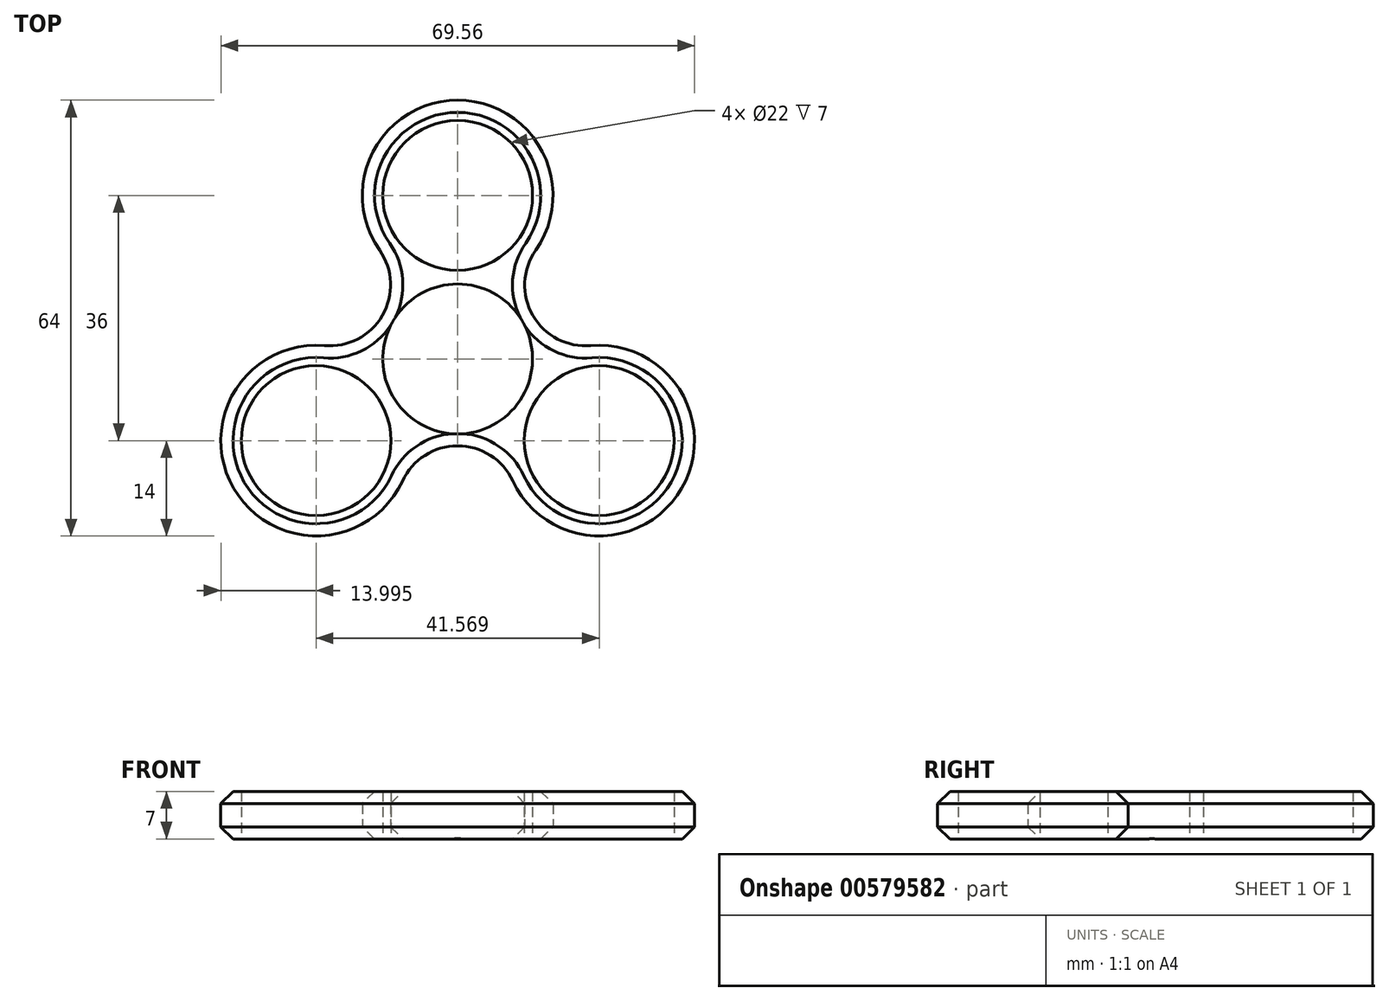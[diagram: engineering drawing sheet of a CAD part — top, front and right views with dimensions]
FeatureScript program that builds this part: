
annotation { "Feature Type Name" : "Feature", "Feature Type Description" : "" }
export const myFeature = defineFeature(function(context is Context, id is Id, definition is map)
    precondition{}
    {
        {
            var Q0;
            Q0=qCreatedBy(makeId("Top.planeOp"),FACE);
            var sketch = newSketch(context, id + "F0", { "sketchPlane" : qUnion([Q0])});
            skCircle(sketch, "E0", {"center": v(0, 0) * mm, "radius": 11 * mm});
            skLineSegment(sketch, "E1", {"start": v(0, 0) * mm, "end": v(0, 11) * mm});
            skCircle(sketch, "E2", {"center": v(0, 24) * mm, "radius": 11 * mm});
            skArc(sketch, "E3.0", {"start": v(11.47, 15.97) * mm, "mid": v(0, 38) * mm, "end": v(-11.47, 15.97) * mm});
            skPoint(sketch, "E4", {"position": v(0, 11) * mm});
            skPoint(sketch, "E5", {"position": v(-12.12, 17) * mm});
            skPoint(sketch, "E6", {"position": v(13, 19.5) * mm});
            skArc(sketch, "E7.1.0", {"start": v(-19.56, 1.95) * mm, "mid": v(-32.9, -19) * mm, "end": v(-8.1, -17.92) * mm});
            skCircle(sketch, "E7.1.1", {"center": v(-20.78, -12) * mm, "radius": 11 * mm});
            skArc(sketch, "E7.2.0", {"start": v(8.1, -17.92) * mm, "mid": v(32.9, -19) * mm, "end": v(19.56, 1.95) * mm});
            skCircle(sketch, "E7.2.1", {"center": v(20.78, -12) * mm, "radius": 11 * mm});
            skPoint(sketch, "E8.1.0", {"position": v(-8.66, -19) * mm});
            skPoint(sketch, "E8.2.0", {"position": v(20.78, 2) * mm});
            skPoint(sketch, "E9.MirrorP", {"position": v(12.12, 17) * mm});
            skPoint(sketch, "E10.1.0", {"position": v(-20.78, 2) * mm});
            skPoint(sketch, "E10.2.0", {"position": v(8.66, -19) * mm});
            skLineSegment(sketch, "E11", {"start": v(-11.05, 6.38) * mm, "end": v(-11.26, 6.5) * mm});
            skPoint(sketch, "E12", {"position": v(-11.26, 6.5) * mm});
            skLineSegment(sketch, "E13", {"start": v(0, 24) * mm, "end": v(-9.01, 17.7) * mm});
            skLineSegment(sketch, "E14.MirrorCS", {"start": v(-20.78, -12) * mm, "end": v(-19.83, -1.04) * mm});
            skPoint(sketch, "E15.orphan", {"position": v(-3.47, 10.44) * mm});
            skArc(sketch, "E16", {"start": v(-11.47, 15.97) * mm, "mid": v(-11.05, 6.38) * mm, "end": v(-19.56, 1.95) * mm});
            skArc(sketch, "E17.1.0", {"start": v(-8.1, -17.92) * mm, "mid": v(0, -12.76) * mm, "end": v(8.1, -17.92) * mm});
            skArc(sketch, "E17.2.0", {"start": v(19.56, 1.95) * mm, "mid": v(11.05, 6.38) * mm, "end": v(11.47, 15.97) * mm});
            skPoint(sketch, "E18.orphan", {"position": v(-10.78, -2.21) * mm});
            skPoint(sketch, "E19.orphan", {"position": v(3.47, 10.44) * mm});
            skPoint(sketch, "E20.orphan", {"position": v(10.78, -2.21) * mm});
            skPoint(sketch, "E21.orphan", {"position": v(7.3, -8.23) * mm});
            skPoint(sketch, "E22.orphan", {"position": v(-7.3, -8.23) * mm});
            skLineSegment(sketch, "E23.trimOffspring", {"start": v(0, 13) * mm, "end": v(0, 24) * mm});
            skSolve(sketch);
        }
        {
            var Q0;
            Q0=makeQuery(id+"F0.imprint","IMPRINT",FACE,{"disambiguationData":[TD([[makeQuery(id+"F0.imprint","IMPRINT",EDGE,{"derivedFrom":sQuery(id+"F0.wireOp",EDGE,"E0")}),-1.0]])]});
            var Q1;
            Q1=makeQuery(id+"F0.imprint","IMPRINT",FACE,{"disambiguationData":[TD([[makeQuery(id+"F0.imprint","IMPRINT",EDGE,{"derivedFrom":sQuery(id+"F0.wireOp",EDGE,"E2")}),-1.0]])]});
            var Q2;
            Q2=makeQuery(id+"F0.imprint","IMPRINT",FACE,{"disambiguationData":[TD([[makeQuery(id+"F0.imprint","IMPRINT",EDGE,{"derivedFrom":sQuery(id+"F0.wireOp",EDGE,"fa5e772c-26e7-4415-bcaa-e380382abe9a.1.1")}),-1.0]])]});
            var Q3;
            Q3=makeQuery(id+"F0.imprint","IMPRINT",FACE,{"disambiguationData":[TD([[makeQuery(id+"F0.imprint","IMPRINT",EDGE,{"derivedFrom":sQuery(id+"F0.wireOp",EDGE,"fa5e772c-26e7-4415-bcaa-e380382abe9a.2.1")}),-1.0]])]});
            extrude(context, id + "F1", {"entities" : qUnion([Q0, Q1, Q2, Q3]), "endBound" : BoundingType.SYMMETRIC, "depth" : 7 * mm, "offsetDistance" : 25 * mm});
        }
        {
            var Q0;
            Q0=makeQuery(id+"F1.opExtrude","CAP_EDGE",EDGE,{"disambiguationData":[OSD([sQuery(id+"F0.wireOp",EDGE,"E7.1.0")])],"isStart":false});
            var Q1;
            Q1=makeQuery(id+"F1.opExtrude","CAP_EDGE",EDGE,{"disambiguationData":[OSD([sQuery(id+"F0.wireOp",EDGE,"E7.1.0")])],"isStart":true});
            chamfer(context, id + "F2", {"entities" : qUnion([Q0, Q1]), "width" : 1.8 * mm, "tangentPropagation" : true});
        }
    });
